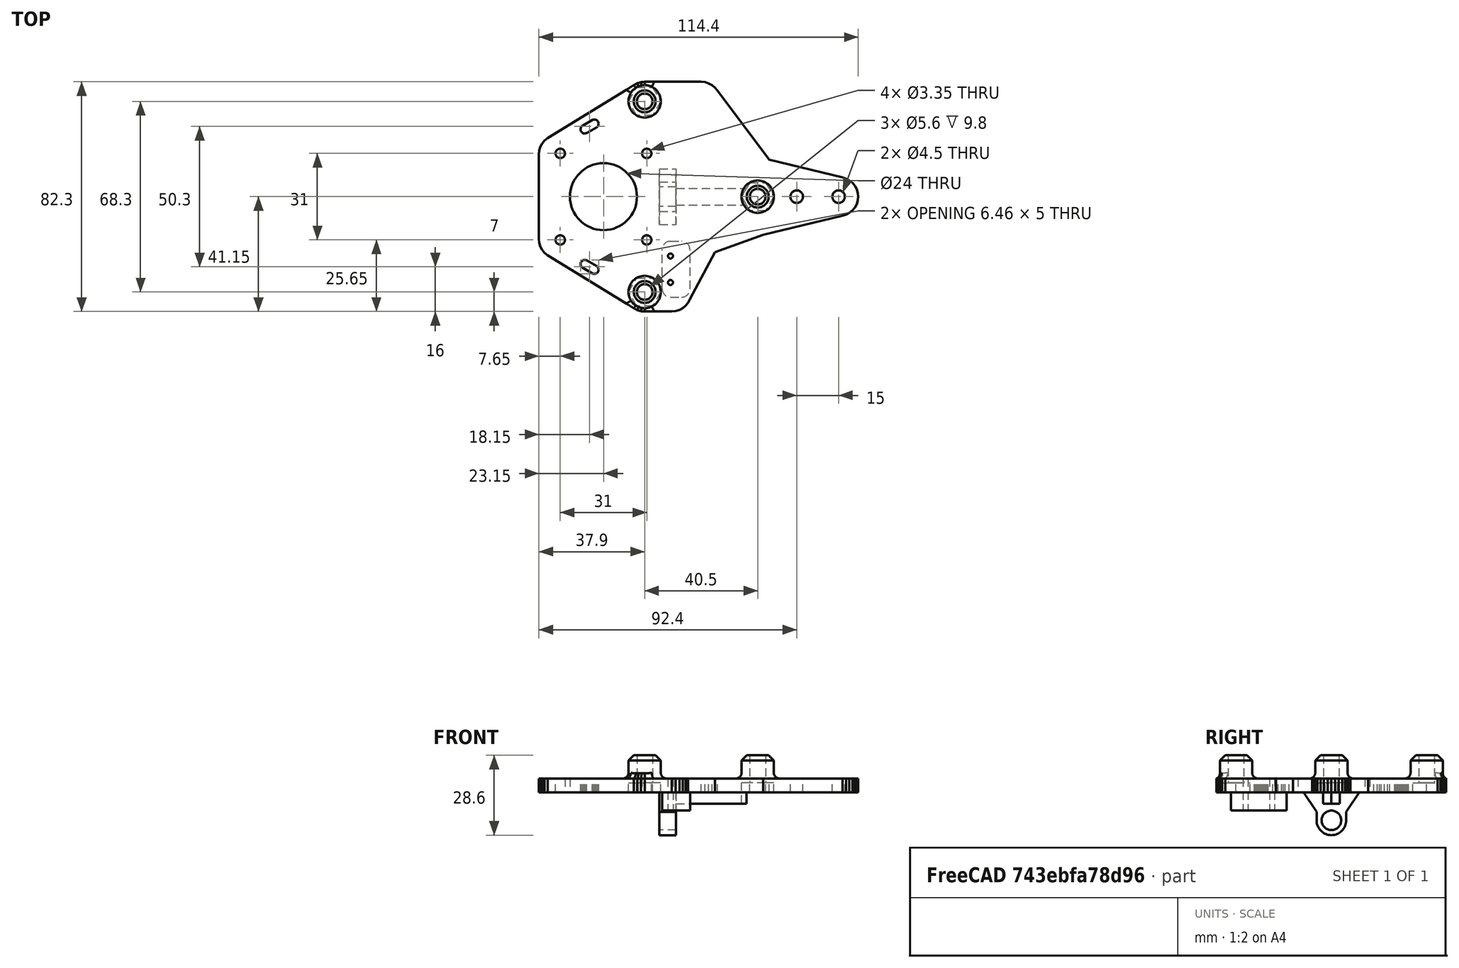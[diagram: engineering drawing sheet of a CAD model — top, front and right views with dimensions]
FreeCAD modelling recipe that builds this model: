
FCSTD DOCUMENT  (FreeCAD 0.19R24267 +99 (Git))
Label: carroZ_0
License: All rights reserved
LicenseURL: http://en.wikipedia.org/wiki/All_rights_reserved
objects: Part::Feature×125, Part::Part2DObjectPython×13, Part::Cylinder×10, Part::Cut×6, Part::FeaturePython×5, Part::Fuse×5, Part::MultiFuse×4, Part::Prism×4, Part::Box×3, Part::Plane×2, Part::Extrusion×2, Part::Fillet×2, Part::Common×1, App::DocumentObjectGroupPython×1, Part::Refine×1, Part::Chamfer×1
note: 184 computed .brp shape members not serialized (recipe doc carries the construction recipe); baked Part::Feature solids carry a one-line shape summary decoded from their .brp

FEATURE [Part::Feature] polygon
  shape: bbox 100.4 x 68.3 x 2e-07 mm, 1 faces, 0 solids (baked)
FEATURE [Part::Part2DObjectPython] circle  # Draft 2D object (typed FeaturePython)
  Area = 153.938
  FirstAngle = 0
  LastAngle = 0
  MakeFace = true
  Radius = 7
FEATURE [Part::FeaturePython] minkowski  # WARN: FeaturePython — macro-defined, semantics opaque (R4)
  Arguments = {'convexity': '0'}
  Children = -> [polygon,circle]
  Operation = minkowski
FEATURE [Part::Part2DObjectPython] circle001  # Draft 2D object (typed FeaturePython)
  Area = 24.6301
  FirstAngle = 0
  LastAngle = 0
  MakeFace = true
  Placement = pos=(-20.25,-34.15,0) rot=(0,0,1;0rad)
  Radius = 2.8
FEATURE [Part::Part2DObjectPython] circle002  # Draft 2D object (typed FeaturePython)
  Area = 24.6301
  FirstAngle = 0
  LastAngle = 0
  MakeFace = true
  Placement = pos=(-20.25,34.15,0) rot=(0,0,1;0rad)
  Radius = 2.8
FEATURE [Part::Part2DObjectPython] circle003  # Draft 2D object (typed FeaturePython)
  Area = 24.6301
  FirstAngle = 0
  LastAngle = 0
  MakeFace = true
  Placement = pos=(20.25,0,0) rot=(0,0,1;0rad)
  Radius = 2.8
FEATURE [Part::Part2DObjectPython] circle004  # Draft 2D object (typed FeaturePython)
  Area = 452.389
  FirstAngle = 0
  LastAngle = 0
  MakeFace = true
  Radius = 12
FEATURE [Part::Part2DObjectPython] circle005  # Draft 2D object (typed FeaturePython)
  Area = 8.81413
  FirstAngle = 0
  LastAngle = 0
  MakeFace = true
  Placement = pos=(15.5,15.5,0) rot=(0,0,1;0rad)
  Radius = 1.675
FEATURE [Part::Part2DObjectPython] circle006  # Draft 2D object (typed FeaturePython)
  Area = 8.81413
  FirstAngle = 0
  LastAngle = 0
  MakeFace = true
  Placement = pos=(-15.5,15.5,0) rot=(0,0,1;1.5708rad)
  Radius = 1.675
FEATURE [Part::Part2DObjectPython] circle007  # Draft 2D object (typed FeaturePython)
  Area = 8.81413
  FirstAngle = 0
  LastAngle = 0
  MakeFace = true
  Placement = pos=(-15.5,-15.5,0) rot=(0,0,1;3.14159rad)
  Radius = 1.675
FEATURE [Part::Part2DObjectPython] circle008  # Draft 2D object (typed FeaturePython)
  Area = 8.81413
  FirstAngle = 0
  LastAngle = 0
  MakeFace = true
  Placement = pos=(15.5,-15.5,0) rot=(0,0,-1;1.5708rad)
  Radius = 1.675
FEATURE [Part::MultiFuse] Group
  Shapes = -> [circle005,circle006,circle007,circle008]
FEATURE [Part::Fuse] Group001
  Base = -> circle004
  Placement = pos=(-35,0,0) rot=(0,0,1;0rad)
  Tool = -> Group
FEATURE [Part::Plane] square
  AttacherType = Attacher::AttachEngine3D
  Length = 4
  Placement = pos=(-2,-0.005,0) rot=(0,0,1;0rad)
  Width = 0.01
FEATURE [Part::Part2DObjectPython] circle009  # Draft 2D object (typed FeaturePython)
  Area = 7.06858
  FirstAngle = 0
  LastAngle = 0
  MakeFace = true
  Radius = 1.5
FEATURE [Part::FeaturePython] minkowski001  # WARN: FeaturePython — macro-defined, semantics opaque (R4)
  Arguments = {'convexity': '0'}
  Children = -> [square,circle009]
  Operation = minkowski
  Placement = pos=(-40,-25.15,0) rot=(0,0,-1;0.523599rad)
FEATURE [Part::Plane] square001
  AttacherType = Attacher::AttachEngine3D
  Length = 4
  Placement = pos=(-2,-0.005,0) rot=(0,0,1;0rad)
  Width = 0.01
FEATURE [Part::Part2DObjectPython] circle010  # Draft 2D object (typed FeaturePython)
  Area = 7.06858
  FirstAngle = 0
  LastAngle = 0
  MakeFace = true
  Radius = 1.5
FEATURE [Part::FeaturePython] minkowski002  # WARN: FeaturePython — macro-defined, semantics opaque (R4)
  Arguments = {'convexity': '0'}
  Children = -> [square001,circle010]
  Operation = minkowski
  Placement = pos=(-40,25.15,0) rot=(0,0,1;0.523599rad)
FEATURE [Part::MultiFuse] union
  Shapes = -> [circle001,circle002,circle003,Group001,minkowski001,minkowski002]
FEATURE [Part::Cut] difference
  Base = -> minkowski
  Tool = -> union
FEATURE [Part::FeaturePython] RefineLinearExtrude  # WARN: FeaturePython — macro-defined, semantics opaque (R4)
  Base = -> difference
FEATURE [Part::Extrusion] LinearExtrude
  Base = -> RefineLinearExtrude
  Dir = (0,0,5)
  DirMode = 0
  FaceMakerClass = Part::FaceMakerBullseye
  LengthFwd = 0
  LengthRev = 0
  Solid = false
  Symmetric = false
FEATURE [Part::Cylinder] cylinder
  Angle = 360
  AttacherType = Attacher::AttachEngine3D
  Height = 13.3
  Radius = 5.8
FEATURE [Part::Cylinder] cylinder001
  Angle = 360
  AttacherType = Attacher::AttachEngine3D
  Height = 53.2
  Placement = pos=(0,0,-26.6) rot=(0,0,1;0rad)
  Radius = 2.8
FEATURE [Part::Cut] difference001
  Base = -> cylinder
  Placement = pos=(-20.25,-34.15,0) rot=(0,0,1;0rad)
  Tool = -> cylinder001
FEATURE [Part::Cylinder] cylinder002
  Angle = 360
  AttacherType = Attacher::AttachEngine3D
  Height = 13.3
  Radius = 5.8
FEATURE [Part::Cylinder] cylinder003
  Angle = 360
  AttacherType = Attacher::AttachEngine3D
  Height = 53.2
  Placement = pos=(0,0,-26.6) rot=(0,0,1;0rad)
  Radius = 2.8
FEATURE [Part::Cut] difference002
  Base = -> cylinder002
  Placement = pos=(-20.25,34.15,0) rot=(0,0,1;0rad)
  Tool = -> cylinder003
FEATURE [Part::Cylinder] cylinder004
  Angle = 360
  AttacherType = Attacher::AttachEngine3D
  Height = 13.3
  Radius = 5.8
FEATURE [Part::Cylinder] cylinder005
  Angle = 360
  AttacherType = Attacher::AttachEngine3D
  Height = 53.2
  Placement = pos=(0,0,-26.6) rot=(0,0,1;0rad)
  Radius = 2.8
FEATURE [Part::Cut] difference003
  Base = -> cylinder004
  Placement = pos=(20.25,0,0) rot=(0,0,1;0rad)
  Tool = -> cylinder005
FEATURE [Part::Box] cube
  AttacherType = Attacher::AttachEngine3D
  Height = 4
  Length = 30.25
  Placement = pos=(-10,-3,-4) rot=(0,0,1;0rad)
  Width = 6
FEATURE [Part::Box] cube001
  AttacherType = Attacher::AttachEngine3D
  Height = 11.5
  Length = 10
  Placement = pos=(-14,-16,5) rot=(1,0,0;3.14159rad)
  Width = 20
FEATURE [Part::MultiFuse] union001
  Shapes = -> [LinearExtrude,difference001,difference002,difference003,cube,cube001]
FEATURE [Part::Prism] prism
  AttacherType = Attacher::AttachEngine3D
  Circumradius = 5.79
  FirstAngle = 0
  Height = 7
  Placement = pos=(-20.25,-34.15,-3.5) rot=(0,0,1;0rad)
  Polygon = 6
  SecondAngle = 0
FEATURE [Part::Prism] prism001
  AttacherType = Attacher::AttachEngine3D
  Circumradius = 5.79
  FirstAngle = 0
  Height = 7
  Placement = pos=(-20.25,34.15,-3.5) rot=(0,0,1;0rad)
  Polygon = 6
  SecondAngle = 0
FEATURE [Part::Prism] prism002
  AttacherType = Attacher::AttachEngine3D
  Circumradius = 5.79
  FirstAngle = 0
  Height = 7
  Placement = pos=(20.25,0,-3.5) rot=(0,0,1;0rad)
  Polygon = 6
  SecondAngle = 0
FEATURE [Part::Prism] prism003
  AttacherType = Attacher::AttachEngine3D
  Circumradius = 5.79
  FirstAngle = 0
  Height = 57
  Placement = pos=(20.25,0,-53.5) rot=(0,0,1;0rad)
  Polygon = 6
  SecondAngle = 0
FEATURE [Part::Cylinder] cylinder006
  Angle = 360
  AttacherType = Attacher::AttachEngine3D
  Height = 15
  Placement = pos=(0,0,-7.5) rot=(0,0,1;0rad)
  Radius = 2.25
FEATURE [Part::Cylinder] cylinder007
  Angle = 360
  AttacherType = Attacher::AttachEngine3D
  Height = 15
  Placement = pos=(15,0,-7.5) rot=(0,0,1;0rad)
  Radius = 2.25
FEATURE [Part::Fuse] Group002
  Base = -> cylinder006
  Placement = pos=(34.25,0,0) rot=(0,0,1;0rad)
  Tool = -> cylinder007
FEATURE [Part::Cylinder] cylinder008
  Angle = 360
  AttacherType = Attacher::AttachEngine3D
  Height = 100
  Placement = pos=(0,0,-50) rot=(0,0,1;0rad)
  Radius = 0.9
FEATURE [Part::Cylinder] cylinder009
  Angle = 360
  AttacherType = Attacher::AttachEngine3D
  Height = 100
  Placement = pos=(0,9.5,-50) rot=(0,0,1;0rad)
  Radius = 0.9
FEATURE [Part::Fuse] Group003
  Base = -> cylinder008
  Placement = pos=(-11,-21.25,5) rot=(1,0,0;3.14159rad)
  Tool = -> cylinder009
FEATURE [Part::MultiFuse] Group004
  Shapes = -> [prism,prism001,prism002,prism003,Group002,Group003]
FEATURE [Part::Cut] difference004
  Base = -> union001
  Tool = -> Group004
FEATURE [Part::Feature] polygon001
  shape: bbox 20 x 10 x 2e-07 mm, 1 faces, 0 solids (baked)
FEATURE [Part::Part2DObjectPython] circle011  # Draft 2D object (typed FeaturePython)
  Area = 88.2473
  FirstAngle = 0
  LastAngle = 0
  MakeFace = true
  Radius = 5.3
FEATURE [Part::Fuse] union002
  Base = -> polygon001
  Tool = -> circle011
FEATURE [Part::Part2DObjectPython] circle012  # Draft 2D object (typed FeaturePython)
  Area = 38.4845
  FirstAngle = 0
  LastAngle = 0
  MakeFace = true
  Radius = 3.5
FEATURE [Part::Cut] difference005
  Base = -> union002
  Placement = pos=(0,0,0) rot=(0,0,-1;1.5708rad)
  Tool = -> circle012
FEATURE [Part::FeaturePython] RefineLinearExtrude001  # WARN: FeaturePython — macro-defined, semantics opaque (R4)
  Base = -> difference005
FEATURE [Part::Extrusion] LinearExtrude001
  Base = -> RefineLinearExtrude001
  Dir = (0,0,6)
  DirMode = 0
  FaceMakerClass = Part::FaceMakerBullseye
  LengthFwd = 0
  LengthRev = 0
  Placement = pos=(-15,0,-10) rot=(0,1,0;1.5708rad)
  Solid = false
  Symmetric = false
FEATURE [Part::Fuse] union003
  Base = -> difference004
  Tool = -> LinearExtrude001
FEATURE [Part::Box] cube002
  AttacherType = Attacher::AttachEngine3D
  Height = 200
  Length = 200
  Placement = pos=(-100,-100,-100) rot=(0,0,1;0rad)
  Width = 200
FEATURE [Part::Common] intersection
  Base = -> union003
  Tool = -> cube002
FEATURE [App::DocumentObjectGroupPython] LayerContainer  label="Capas"  # scripted group (container) (typed FeaturePython)
FEATURE [Part::Feature] Line
  shape: bbox 1.313 x 0.3984 x 2e-07 mm, 0 faces, 0 solids (baked)
FEATURE [Part::Feature] Line001
  shape: bbox 1.365 x 0.1348 x 2e-07 mm, 0 faces, 0 solids (baked)
FEATURE [Part::Feature] Line002
  shape: bbox 20.25 x 2e-07 x 2e-07 mm, 0 faces, 0 solids (baked)
FEATURE [Part::Feature] Line003
  shape: bbox 1.365 x 0.1348 x 2e-07 mm, 0 faces, 0 solids (baked)
FEATURE [Part::Feature] Line004
  shape: bbox 1.314 x 0.3984 x 2e-07 mm, 0 faces, 0 solids (baked)
FEATURE [Part::Feature] Line005
  shape: bbox 1.21 x 0.6465 x 2e-07 mm, 0 faces, 0 solids (baked)
FEATURE [Part::Feature] Line006
  shape: bbox 30.9 x 19 x 2e-07 mm, 0 faces, 0 solids (baked)
FEATURE [Part::Feature] Line007
  shape: bbox 1.062 x 0.8701 x 2e-07 mm, 0 faces, 0 solids (baked)
FEATURE [Part::Feature] Line008
  shape: bbox 0.8701 x 1.062 x 2e-07 mm, 0 faces, 0 solids (baked)
FEATURE [Part::Feature] Line009
  shape: bbox 0.6465 x 1.21 x 2e-07 mm, 0 faces, 0 solids (baked)
FEATURE [Part::Feature] Line010
  shape: bbox 0.3984 x 1.314 x 2e-07 mm, 0 faces, 0 solids (baked)
FEATURE [Part::Feature] Line011
  shape: bbox 0.1348 x 1.365 x 2e-07 mm, 0 faces, 0 solids (baked)
FEATURE [Part::Feature] Line012
  shape: bbox 2e-07 x 30.3 x 2e-07 mm, 0 faces, 0 solids (baked)
FEATURE [Part::Feature] Line013
  shape: bbox 0.1348 x 1.365 x 2e-07 mm, 0 faces, 0 solids (baked)
FEATURE [Part::Feature] Line014
  shape: bbox 0.3984 x 1.314 x 2e-07 mm, 0 faces, 0 solids (baked)
FEATURE [Part::Feature] Line015
  shape: bbox 0.6465 x 1.21 x 2e-07 mm, 0 faces, 0 solids (baked)
FEATURE [Part::Feature] Line016
  shape: bbox 0.8701 x 1.062 x 2e-07 mm, 0 faces, 0 solids (baked)
FEATURE [Part::Feature] Line017
  shape: bbox 1.062 x 0.8701 x 2e-07 mm, 0 faces, 0 solids (baked)
FEATURE [Part::Feature] Line018
  shape: bbox 30.9 x 19 x 2e-07 mm, 0 faces, 0 solids (baked)
FEATURE [Part::Feature] Line019
  shape: bbox 1.21 x 0.6465 x 2e-07 mm, 0 faces, 0 solids (baked)
FEATURE [Part::Feature] Line020
  shape: bbox 1.314 x 0.3984 x 2e-07 mm, 0 faces, 0 solids (baked)
FEATURE [Part::Feature] Line021
  shape: bbox 1.365 x 0.1348 x 2e-07 mm, 0 faces, 0 solids (baked)
FEATURE [Part::Feature] Line022
  shape: bbox 9.75 x 2e-07 x 2e-07 mm, 0 faces, 0 solids (baked)
FEATURE [Part::Feature] Line023
  shape: bbox 1.365 x 0.1348 x 2e-07 mm, 0 faces, 0 solids (baked)
FEATURE [Part::Feature] Line024
  shape: bbox 1.313 x 0.3984 x 2e-07 mm, 0 faces, 0 solids (baked)
FEATURE [Part::Feature] Line025
  shape: bbox 1.21 x 0.6465 x 2e-07 mm, 0 faces, 0 solids (baked)
FEATURE [Part::Feature] Line026
  shape: bbox 1.062 x 0.8701 x 2e-07 mm, 0 faces, 0 solids (baked)
FEATURE [Part::Feature] Line027
  shape: bbox 0.8701 x 1.062 x 2e-07 mm, 0 faces, 0 solids (baked)
FEATURE [Part::Feature] Line028
  shape: bbox 0.6465 x 1.21 x 2e-07 mm, 0 faces, 0 solids (baked)
FEATURE [Part::Feature] Line029
  shape: bbox 8.921 x 16.99 x 2e-07 mm, 0 faces, 0 solids (baked)
FEATURE [Part::Feature] Line030
  shape: bbox 17.31 x 6.113 x 2e-07 mm, 0 faces, 0 solids (baked)
FEATURE [Part::Feature] Line031
  shape: bbox 28.42 x 6.859 x 2e-07 mm, 0 faces, 0 solids (baked)
FEATURE [Part::Feature] Line032
  shape: bbox 1.314 x 0.3984 x 2e-07 mm, 0 faces, 0 solids (baked)
FEATURE [Part::Feature] Line033
  shape: bbox 1.21 x 0.6465 x 2e-07 mm, 0 faces, 0 solids (baked)
FEATURE [Part::Feature] Line034
  shape: bbox 1.062 x 0.8701 x 2e-07 mm, 0 faces, 0 solids (baked)
FEATURE [Part::Feature] Line035
  shape: bbox 0.8701 x 1.062 x 2e-07 mm, 0 faces, 0 solids (baked)
FEATURE [Part::Feature] Line036
  shape: bbox 0.6465 x 1.21 x 2e-07 mm, 0 faces, 0 solids (baked)
FEATURE [Part::Feature] Line037
  shape: bbox 0.3984 x 1.313 x 2e-07 mm, 0 faces, 0 solids (baked)
FEATURE [Part::Feature] Line038
  shape: bbox 0.1348 x 1.365 x 2e-07 mm, 0 faces, 0 solids (baked)
FEATURE [Part::Feature] Line039
  shape: bbox 0.1348 x 1.365 x 2e-07 mm, 0 faces, 0 solids (baked)
FEATURE [Part::Feature] Line040
  shape: bbox 0.3984 x 1.313 x 2e-07 mm, 0 faces, 0 solids (baked)
FEATURE [Part::Feature] Line041
  shape: bbox 0.6465 x 1.21 x 2e-07 mm, 0 faces, 0 solids (baked)
FEATURE [Part::Feature] Line042
  shape: bbox 0.8701 x 1.062 x 2e-07 mm, 0 faces, 0 solids (baked)
FEATURE [Part::Feature] Line043
  shape: bbox 1.062 x 0.8701 x 2e-07 mm, 0 faces, 0 solids (baked)
FEATURE [Part::Feature] Line044
  shape: bbox 1.21 x 0.6465 x 2e-07 mm, 0 faces, 0 solids (baked)
FEATURE [Part::Feature] Line045
  shape: bbox 1.314 x 0.3984 x 2e-07 mm, 0 faces, 0 solids (baked)
FEATURE [Part::Feature] Line046
  shape: bbox 26.27 x 6.342 x 2e-07 mm, 0 faces, 0 solids (baked)
FEATURE [Part::Feature] Line047
  shape: bbox 18.52 x 24.83 x 2e-07 mm, 0 faces, 0 solids (baked)
FEATURE [Part::Feature] Line048
  shape: bbox 0.8701 x 1.062 x 2e-07 mm, 0 faces, 0 solids (baked)
FEATURE [Part::Feature] Line049
  shape: bbox 1.062 x 0.8701 x 2e-07 mm, 0 faces, 0 solids (baked)
FEATURE [Part::Feature] Line050
  shape: bbox 1.21 x 0.6465 x 2e-07 mm, 0 faces, 0 solids (baked)
FEATURE [Part::Feature] Line051
  shape: bbox 0.2275 x 0.1865 x 2e-07 mm, 0 faces, 0 solids (baked)
FEATURE [Part::Feature] Line052
  shape: bbox 0.1865 x 0.2275 x 2e-07 mm, 0 faces, 0 solids (baked)
FEATURE [Part::Feature] Line053
  shape: bbox 0.1387 x 0.2588 x 2e-07 mm, 0 faces, 0 solids (baked)
FEATURE [Part::Feature] Line054
  shape: bbox 0.08496 x 0.2813 x 2e-07 mm, 0 faces, 0 solids (baked)
FEATURE [Part::Feature] Line055
  shape: bbox 0.0293 x 0.293 x 2e-07 mm, 0 faces, 0 solids (baked)
FEATURE [Part::Feature] Line056
  shape: bbox 2e-07 x 0.009766 x 2e-07 mm, 0 faces, 0 solids (baked)
FEATURE [Part::Feature] Line057
  shape: bbox 0.0293 x 0.293 x 2e-07 mm, 0 faces, 0 solids (baked)
FEATURE [Part::Feature] Line058
  shape: bbox 0.08496 x 0.2813 x 2e-07 mm, 0 faces, 0 solids (baked)
FEATURE [Part::Feature] Line059
  shape: bbox 0.1387 x 0.2588 x 2e-07 mm, 0 faces, 0 solids (baked)
FEATURE [Part::Feature] Line060
  shape: bbox 0.1865 x 0.2275 x 2e-07 mm, 0 faces, 0 solids (baked)
FEATURE [Part::Feature] Line061
  shape: bbox 0.2275 x 0.1865 x 2e-07 mm, 0 faces, 0 solids (baked)
FEATURE [Part::Feature] Line062
  shape: bbox 0.2588 x 0.1387 x 2e-07 mm, 0 faces, 0 solids (baked)
FEATURE [Part::Feature] Line063
  shape: bbox 0.2813 x 0.08497 x 2e-07 mm, 0 faces, 0 solids (baked)
FEATURE [Part::Feature] Line064
  shape: bbox 0.293 x 0.02929 x 2e-07 mm, 0 faces, 0 solids (baked)
FEATURE [Part::Feature] Line065
  shape: bbox 4 x 2e-07 x 2e-07 mm, 0 faces, 0 solids (baked)
FEATURE [Part::Feature] Line066
  shape: bbox 0.293 x 0.02929 x 2e-07 mm, 0 faces, 0 solids (baked)
FEATURE [Part::Feature] Line067
  shape: bbox 0.2813 x 0.08497 x 2e-07 mm, 0 faces, 0 solids (baked)
FEATURE [Part::Feature] Line068
  shape: bbox 0.2588 x 0.1387 x 2e-07 mm, 0 faces, 0 solids (baked)
FEATURE [Part::Feature] Line069
  shape: bbox 0.2275 x 0.1865 x 2e-07 mm, 0 faces, 0 solids (baked)
FEATURE [Part::Feature] Line070
  shape: bbox 0.1865 x 0.2275 x 2e-07 mm, 0 faces, 0 solids (baked)
FEATURE [Part::Feature] Line071
  shape: bbox 0.1387 x 0.2588 x 2e-07 mm, 0 faces, 0 solids (baked)
FEATURE [Part::Feature] Line072
  shape: bbox 0.08496 x 0.2813 x 2e-07 mm, 0 faces, 0 solids (baked)
FEATURE [Part::Feature] Line073
  shape: bbox 0.0293 x 0.293 x 2e-07 mm, 0 faces, 0 solids (baked)
FEATURE [Part::Feature] Line074
  shape: bbox 2e-07 x 0.009766 x 2e-07 mm, 0 faces, 0 solids (baked)
FEATURE [Part::Feature] Line075
  shape: bbox 0.0293 x 0.293 x 2e-07 mm, 0 faces, 0 solids (baked)
FEATURE [Part::Feature] Line076
  shape: bbox 0.08496 x 0.2813 x 2e-07 mm, 0 faces, 0 solids (baked)
FEATURE [Part::Feature] Line077
  shape: bbox 0.1387 x 0.2588 x 2e-07 mm, 0 faces, 0 solids (baked)
FEATURE [Part::Feature] Line078
  shape: bbox 0.1865 x 0.2275 x 2e-07 mm, 0 faces, 0 solids (baked)
FEATURE [Part::Feature] Line079
  shape: bbox 0.2275 x 0.1865 x 2e-07 mm, 0 faces, 0 solids (baked)
FEATURE [Part::Feature] Line080
  shape: bbox 0.2588 x 0.1387 x 2e-07 mm, 0 faces, 0 solids (baked)
FEATURE [Part::Feature] Line081
  shape: bbox 0.2813 x 0.08497 x 2e-07 mm, 0 faces, 0 solids (baked)
FEATURE [Part::Feature] Line082
  shape: bbox 0.293 x 0.02929 x 2e-07 mm, 0 faces, 0 solids (baked)
FEATURE [Part::Feature] Line083
  shape: bbox 4 x 2e-07 x 2e-07 mm, 0 faces, 0 solids (baked)
FEATURE [Part::Feature] Line084
  shape: bbox 0.293 x 0.02929 x 2e-07 mm, 0 faces, 0 solids (baked)
FEATURE [Part::Feature] Line085
  shape: bbox 0.2813 x 0.08497 x 2e-07 mm, 0 faces, 0 solids (baked)
FEATURE [Part::Feature] Line086
  shape: bbox 0.2588 x 0.1387 x 2e-07 mm, 0 faces, 0 solids (baked)
FEATURE [Part::Feature] Line087
  shape: bbox 0.2275 x 0.1865 x 2e-07 mm, 0 faces, 0 solids (baked)
FEATURE [Part::Feature] Line088
  shape: bbox 0.1865 x 0.2275 x 2e-07 mm, 0 faces, 0 solids (baked)
FEATURE [Part::Feature] Line089
  shape: bbox 0.1387 x 0.2588 x 2e-07 mm, 0 faces, 0 solids (baked)
FEATURE [Part::Feature] Line090
  shape: bbox 0.08496 x 0.2813 x 2e-07 mm, 0 faces, 0 solids (baked)
FEATURE [Part::Feature] Line091
  shape: bbox 0.0293 x 0.293 x 2e-07 mm, 0 faces, 0 solids (baked)
FEATURE [Part::Feature] Line092
  shape: bbox 2e-07 x 0.009766 x 2e-07 mm, 0 faces, 0 solids (baked)
FEATURE [Part::Feature] Line093
  shape: bbox 0.0293 x 0.293 x 2e-07 mm, 0 faces, 0 solids (baked)
FEATURE [Part::Feature] Line094
  shape: bbox 0.08496 x 0.2813 x 2e-07 mm, 0 faces, 0 solids (baked)
FEATURE [Part::Feature] Line095
  shape: bbox 0.1387 x 0.2588 x 2e-07 mm, 0 faces, 0 solids (baked)
FEATURE [Part::Feature] Line096
  shape: bbox 0.1865 x 0.2275 x 2e-07 mm, 0 faces, 0 solids (baked)
FEATURE [Part::Feature] Line097
  shape: bbox 0.2275 x 0.1865 x 2e-07 mm, 0 faces, 0 solids (baked)
FEATURE [Part::Feature] Line098
  shape: bbox 0.2588 x 0.1387 x 2e-07 mm, 0 faces, 0 solids (baked)
FEATURE [Part::Feature] Line099
  shape: bbox 0.2813 x 0.08497 x 2e-07 mm, 0 faces, 0 solids (baked)
FEATURE [Part::Feature] Line100
  shape: bbox 0.293 x 0.02929 x 2e-07 mm, 0 faces, 0 solids (baked)
FEATURE [Part::Feature] Line101
  shape: bbox 4 x 2e-07 x 2e-07 mm, 0 faces, 0 solids (baked)
FEATURE [Part::Feature] Line102
  shape: bbox 0.293 x 0.02929 x 2e-07 mm, 0 faces, 0 solids (baked)
FEATURE [Part::Feature] Line103
  shape: bbox 0.2813 x 0.08497 x 2e-07 mm, 0 faces, 0 solids (baked)
FEATURE [Part::Feature] Line104
  shape: bbox 0.2588 x 0.1387 x 2e-07 mm, 0 faces, 0 solids (baked)
FEATURE [Part::Feature] Line105
  shape: bbox 0.2275 x 0.1865 x 2e-07 mm, 0 faces, 0 solids (baked)
FEATURE [Part::Feature] Line106
  shape: bbox 0.1865 x 0.2275 x 2e-07 mm, 0 faces, 0 solids (baked)
FEATURE [Part::Feature] Line107
  shape: bbox 0.1387 x 0.2588 x 2e-07 mm, 0 faces, 0 solids (baked)
FEATURE [Part::Feature] Line108
  shape: bbox 0.08496 x 0.2813 x 2e-07 mm, 0 faces, 0 solids (baked)
FEATURE [Part::Feature] Line109
  shape: bbox 0.0293 x 0.293 x 2e-07 mm, 0 faces, 0 solids (baked)
FEATURE [Part::Feature] Line110
  shape: bbox 2e-07 x 0.009766 x 2e-07 mm, 0 faces, 0 solids (baked)
FEATURE [Part::Feature] Line111
  shape: bbox 0.0293 x 0.293 x 2e-07 mm, 0 faces, 0 solids (baked)
FEATURE [Part::Feature] Line112
  shape: bbox 0.08496 x 0.2813 x 2e-07 mm, 0 faces, 0 solids (baked)
FEATURE [Part::Feature] Line113
  shape: bbox 0.1387 x 0.2588 x 2e-07 mm, 0 faces, 0 solids (baked)
FEATURE [Part::Feature] Line114
  shape: bbox 0.1865 x 0.2275 x 2e-07 mm, 0 faces, 0 solids (baked)
FEATURE [Part::Feature] Line115
  shape: bbox 0.2275 x 0.1865 x 2e-07 mm, 0 faces, 0 solids (baked)
FEATURE [Part::Feature] Line116
  shape: bbox 0.2588 x 0.1387 x 2e-07 mm, 0 faces, 0 solids (baked)
FEATURE [Part::Feature] Line117
  shape: bbox 0.2813 x 0.08497 x 2e-07 mm, 0 faces, 0 solids (baked)
FEATURE [Part::Feature] Line118
  shape: bbox 0.293 x 0.02929 x 2e-07 mm, 0 faces, 0 solids (baked)
FEATURE [Part::Feature] Line119
  shape: bbox 4 x 2e-07 x 2e-07 mm, 0 faces, 0 solids (baked)
FEATURE [Part::Feature] Line120
  shape: bbox 0.293 x 0.02929 x 2e-07 mm, 0 faces, 0 solids (baked)
FEATURE [Part::Feature] Line121
  shape: bbox 0.2813 x 0.08497 x 2e-07 mm, 0 faces, 0 solids (baked)
FEATURE [Part::Feature] Line122
  shape: bbox 0.2588 x 0.1387 x 2e-07 mm, 0 faces, 0 solids (baked)
FEATURE [Part::Refine] intersection001
  Source = -> intersection
FEATURE [Part::Chamfer] Chamfer
  Base = -> intersection001
  Edges = 3 edges r=1.9: [Edge503,Edge506,Edge509]
FEATURE [Part::Fillet] Fillet
  Base = -> Chamfer
  Edges = 3 edges r=2: [Edge3,Edge58,Edge59]
FEATURE [Part::Fillet] Fillet001
  Base = -> Fillet
  Edges = 4 edges r=3: [Edge521,Edge522,Edge523,Edge524]
